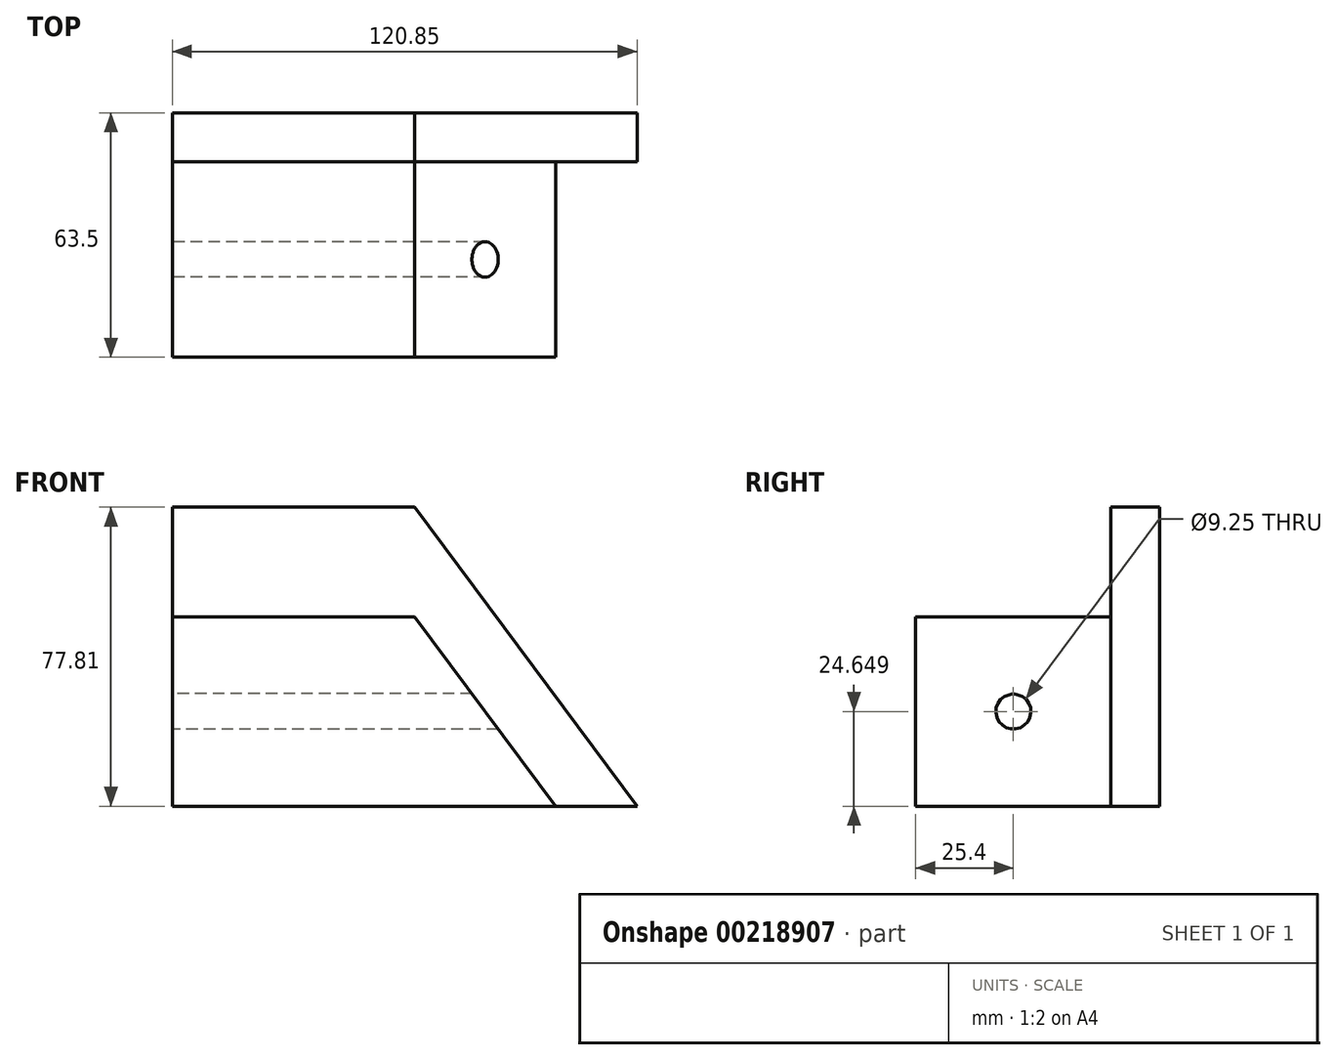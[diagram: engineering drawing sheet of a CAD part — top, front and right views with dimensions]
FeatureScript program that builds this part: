
annotation { "Feature Type Name" : "Feature", "Feature Type Description" : "" }
export const myFeature = defineFeature(function(context is Context, id is Id, definition is map)
    precondition{}
    {
        {
            var Q0;
            Q0=qCreatedBy(makeId("Front.planeOp"),FACE);
            var sketch = newSketch(context, id + "F0", { "sketchPlane" : qUnion([Q0])});
            skLineSegment(sketch, "E0", {"start": v(0, 0) * mm, "end": v(-57.83, 77.8) * mm});
            skLineSegment(sketch, "E1", {"start": v(-57.83, 77.8) * mm, "end": v(-120.85, 77.8) * mm});
            skLineSegment(sketch, "E2", {"start": v(-120.85, 77.8) * mm, "end": v(-120.85, 0) * mm});
            skLineSegment(sketch, "E3", {"start": v(-120.85, 0) * mm, "end": v(0, 0) * mm});
            skSolve(sketch);
        }
        {
            var Q0;
            Q0=makeQuery(id+"F0.imprint","IMPRINT",FACE,{"disambiguationData":[TD([[makeQuery(id+"F0.imprint","IMPRINT",EDGE,{"derivedFrom":sQuery(id+"F0.wireOp",EDGE,"E0")}),1.0]])]});
            extrude(context, id + "F1", {"entities" : qUnion([Q0]), "depth" : 12.7 * mm});
        }
        {
            var Q0;
            Q0=makeQuery(id+"F1.opExtrude","CAP_FACE",FACE,{"disambiguationData":[OSD([sQuery(id+"F0.wireOp",EDGE,"E0"),sQuery(id+"F0.wireOp",EDGE,"E1"),sQuery(id+"F0.wireOp",EDGE,"E2"),sQuery(id+"F0.wireOp",EDGE,"E3")])],"isStart":false});
            var sketch = newSketch(context, id + "F2", { "sketchPlane" : qUnion([Q0])});
            skLineSegment(sketch, "E4", {"start": v(-120.85, 49.3) * mm, "end": v(-57.83, 49.3) * mm});
            skLineSegment(sketch, "E5", {"start": v(-57.83, 49.3) * mm, "end": v(-21.19, 0) * mm});
            skSolve(sketch);
        }
        {
            var Q0;
            {var subQ0=sQuery(id+"F2.wireOp",EDGE,"E4");Q0=makeQuery(id+"F2.imprint","IMPRINT",FACE,{"disambiguationData":[TD([[makeQuery(id+"F2.imprint","IMPRINT",EDGE,{"derivedFrom":subQ0}),-1.0]])]});}
            extrude(context, id + "F3", {"entities" : qUnion([Q0]), "operationType" : NewBodyOperationType.ADD, "depth" : 50.8 * mm});
        }
        {
            var Q0;
            {var subQ0=sQuery(id+"F0.wireOp",EDGE,"E2");Q0=makeQuery(id+"F3.boolean.opBoolean","MERGE",FACE,{"derivedFrom":[makeQuery(id+"F1.opExtrude","SWEPT_FACE",FACE,{"disambiguationData":[OSD([subQ0])]}),makeQuery(id+"F3.opExtrude","SWEPT_FACE",FACE,{"disambiguationData":[OSD([subQ0])]})]});}
            var sketch = newSketch(context, id + "F4", { "sketchPlane" : qUnion([Q0])});
            skCircle(sketch, "E6", {"center": v(38.1, 24.65) * mm, "radius": 4.62 * mm});
            skPoint(sketch, "E6.centerSnap0", {"position": v(63.5, 24.65) * mm});
            skPoint(sketch, "E6.centerSnap1", {"position": v(38.1, 49.3) * mm});
            skSolve(sketch);
        }
        {
            var Q0;
            Q0=makeQuery(id+"F4.imprint","IMPRINT",FACE,{"disambiguationData":[TD([[makeQuery(id+"F4.imprint","IMPRINT",EDGE,{"derivedFrom":sQuery(id+"F4.wireOp",EDGE,"E6")}),1.0]])]});
            extrude(context, id + "F5", {"entities" : qUnion([Q0]), "operationType" : NewBodyOperationType.REMOVE, "endBound" : BoundingType.THROUGH_ALL, "oppositeDirection" : true, "depth" : 25.4 * mm});
        }
    });
